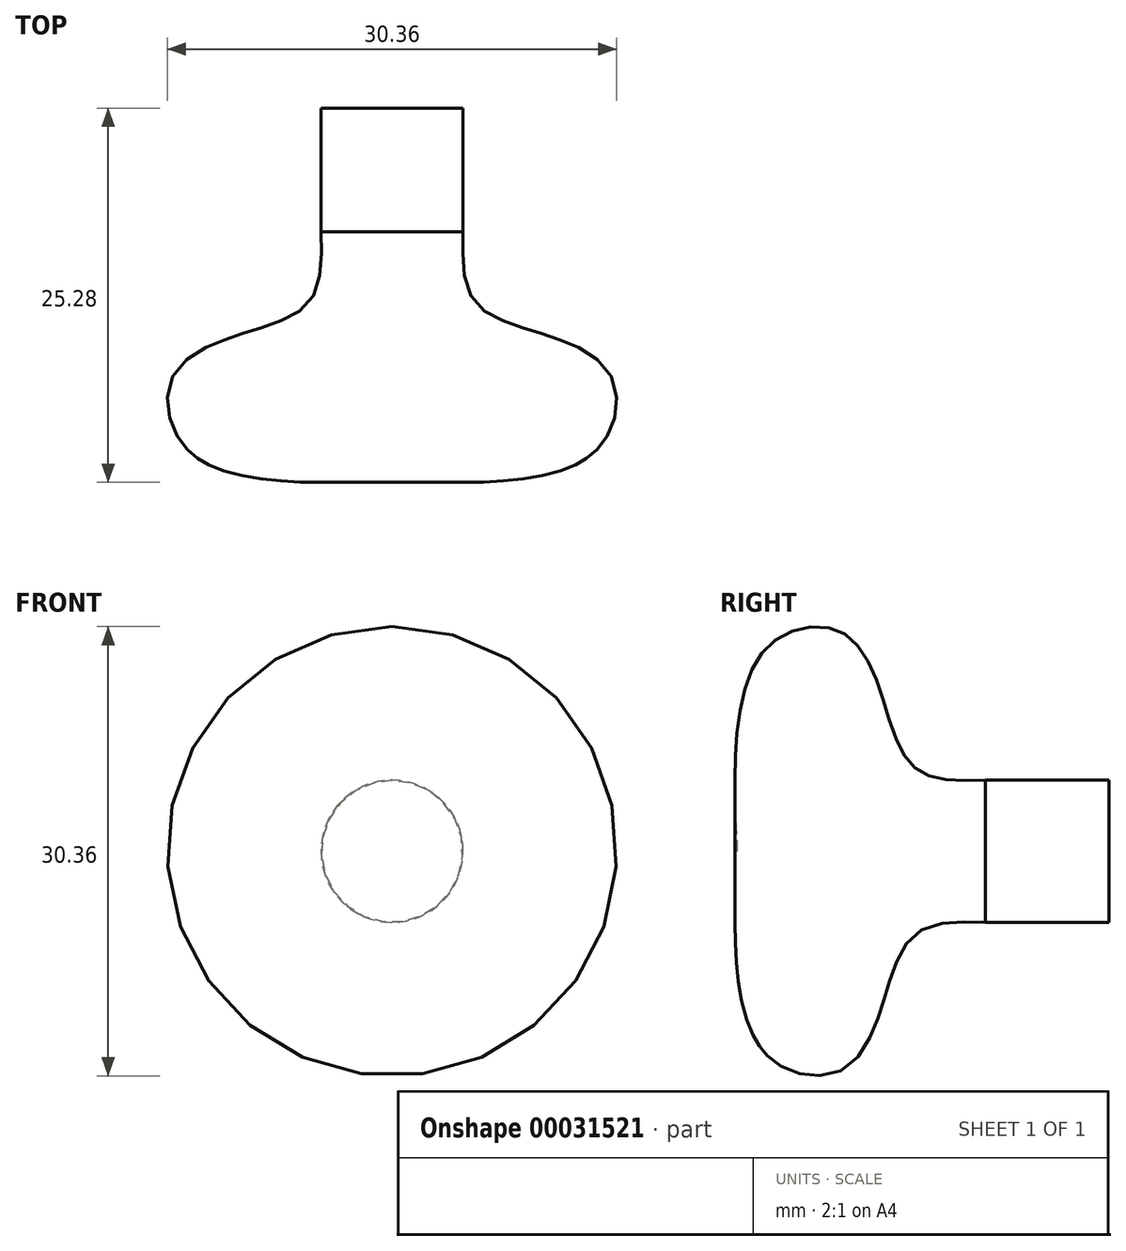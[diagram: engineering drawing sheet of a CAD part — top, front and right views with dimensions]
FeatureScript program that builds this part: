
annotation { "Feature Type Name" : "Feature", "Feature Type Description" : "" }
export const myFeature = defineFeature(function(context is Context, id is Id, definition is map)
    precondition{}
    {
        {
            var Q0;
            Q0=qCreatedBy(makeId("Right.planeOp"),FACE);
            var sketch = newSketch(context, id + "F0", { "sketchPlane" : qUnion([Q0])});
            skLineSegment(sketch, "E0", {"start": v(0, 0) * mm, "end": v(-25.11, 0) * mm});
            skLineSegment(sketch, "E1", {"start": v(0, 0) * mm, "end": v(0, 4.8) * mm});
            skLineSegment(sketch, "E2", {"start": v(0, 4.8) * mm, "end": v(-8.36, 4.8) * mm});
            skFitSpline(sketch, "E3", {"points": [v(-25.11, 0) * mm, v(-25.11, 8.32) * mm, v(-22.82, 14.07) * mm, v(-18.2, 14.86) * mm, v(-15.38, 10.57) * mm, v(-13.12, 5.61) * mm, v(-8.36, 4.8) * mm], "startDerivative": vector(-2.14, 42.8) * mm, "endDerivative": vector(36.3, 0.9) * mm});
            skSolve(sketch);
        }
        {
            var Q0;
            Q0 = qSketchRegion(id + "F0", true);
            var Q1;
            Q1=sQuery(id+"F0.wireOp",EDGE,"E0");
            revolve(context, id + "F1", {"entities" : qUnion([Q0]), "axis" : qUnion([Q1]), "revolveType" : RevolveType.FULL});
        }
    });
